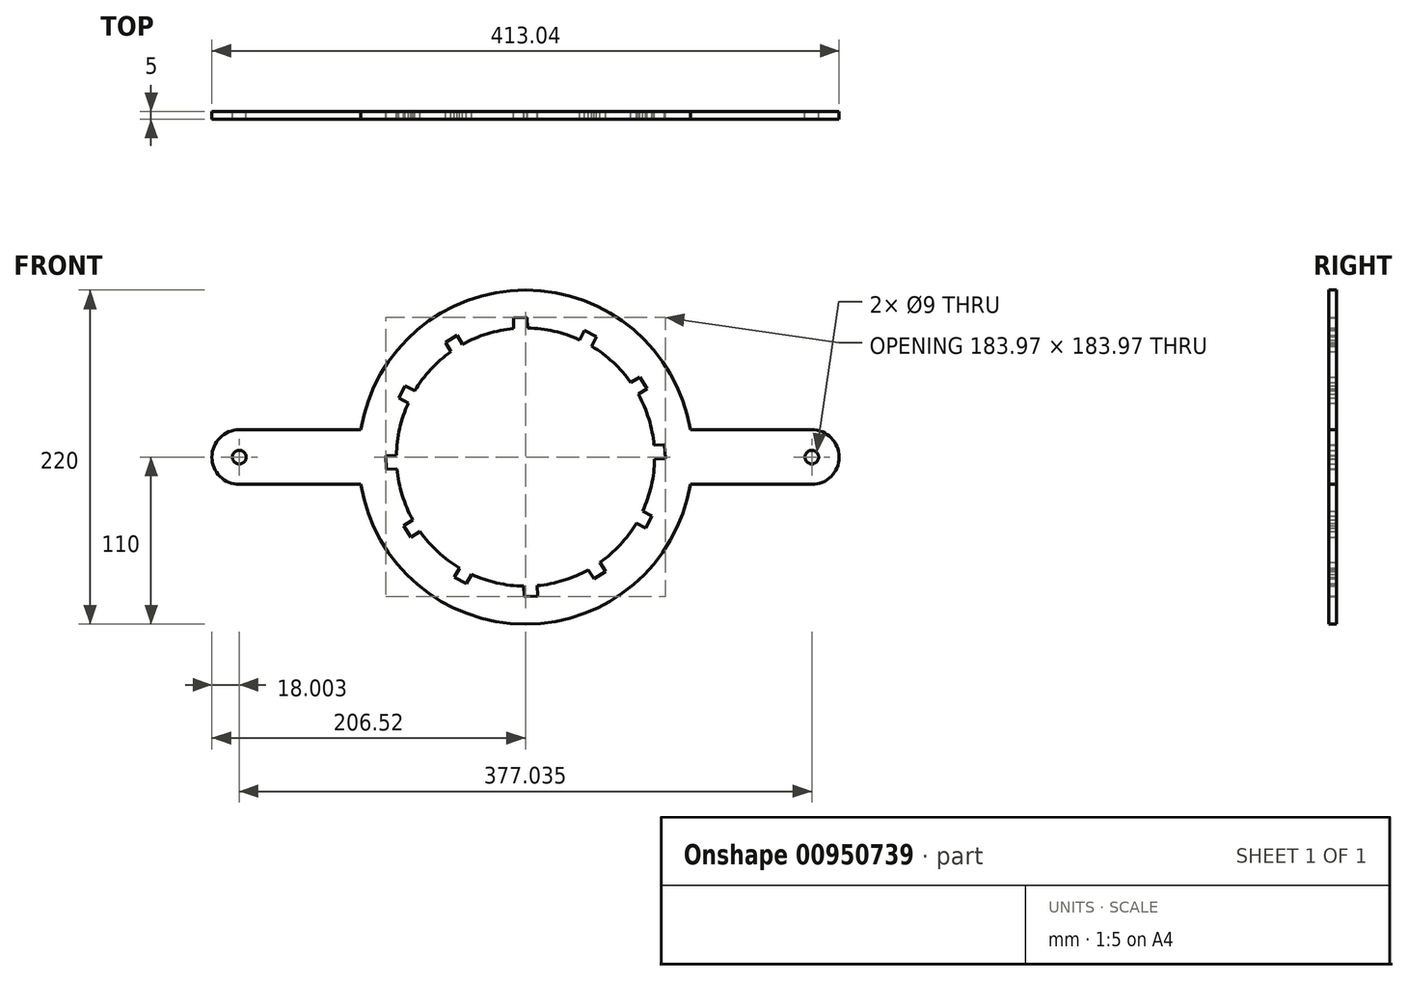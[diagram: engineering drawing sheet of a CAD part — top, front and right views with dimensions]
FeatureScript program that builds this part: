
annotation { "Feature Type Name" : "Feature", "Feature Type Description" : "" }
export const myFeature = defineFeature(function(context is Context, id is Id, definition is map)
    precondition{}
    {
        {
            var Q0;
            Q0=qCreatedBy(makeId("Front.planeOp"),FACE);
            var sketch = newSketch(context, id + "F0", { "sketchPlane" : qUnion([Q0])});
            skArc(sketch, "E0", {"start": v(-77.18, 35.61) * mm, "mid": v(-82.89, 18.84) * mm, "end": v(-85, 1.24) * mm});
            skArc(sketch, "E1", {"start": v(108.52, 18) * mm, "mid": v(0, 110) * mm, "end": v(-108.52, 18) * mm});
            skLineSegment(sketch, "E2", {"start": v(0, 235.77) * mm, "end": v(0, -237.42) * mm, "construction": true});
            skLineSegment(sketch, "E3", {"start": v(-150.79, 0) * mm, "end": v(256.18, 0) * mm, "construction": true});
            skLineSegment(sketch, "E4", {"start": v(-72.98, 43.57) * mm, "end": v(-79.17, 46.84) * mm});
            skLineSegment(sketch, "E5", {"start": v(-79.17, 46.84) * mm, "end": v(-83.37, 38.88) * mm});
            skLineSegment(sketch, "E6", {"start": v(-83.37, 38.88) * mm, "end": v(-77.18, 35.61) * mm});
            skLineSegment(sketch, "E7", {"start": v(-109.8, 57.9) * mm, "end": v(-60.63, 31.97) * mm, "construction": true});
            skLineSegment(sketch, "E8.1.0", {"start": v(-124.05, -4.76) * mm, "end": v(-68.5, -2.63) * mm, "construction": true});
            skLineSegment(sketch, "E8.1.1", {"start": v(-85, 1.24) * mm, "end": v(-91.99, 0.98) * mm});
            skLineSegment(sketch, "E8.1.2", {"start": v(-91.99, 0.98) * mm, "end": v(-91.64, -8.02) * mm});
            skLineSegment(sketch, "E8.1.3", {"start": v(-91.64, -8.02) * mm, "end": v(-84.65, -7.75) * mm});
            skLineSegment(sketch, "E8.2.0", {"start": v(-105.05, -66.15) * mm, "end": v(-58, -36.52) * mm, "construction": true});
            skLineSegment(sketch, "E8.2.1", {"start": v(-74.23, -41.42) * mm, "end": v(-80.15, -45.15) * mm});
            skLineSegment(sketch, "E8.2.2", {"start": v(-80.15, -45.15) * mm, "end": v(-75.35, -52.76) * mm});
            skLineSegment(sketch, "E8.2.3", {"start": v(-75.35, -52.76) * mm, "end": v(-69.43, -49.03) * mm});
            skLineSegment(sketch, "E8.3.0", {"start": v(-57.9, -109.8) * mm, "end": v(-31.97, -60.63) * mm, "construction": true});
            skLineSegment(sketch, "E8.3.1", {"start": v(-43.57, -72.98) * mm, "end": v(-46.84, -79.17) * mm});
            skLineSegment(sketch, "E8.3.2", {"start": v(-46.84, -79.17) * mm, "end": v(-38.88, -83.37) * mm});
            skLineSegment(sketch, "E8.3.3", {"start": v(-38.88, -83.37) * mm, "end": v(-35.61, -77.18) * mm});
            skLineSegment(sketch, "E8.4.0", {"start": v(4.76, -124.05) * mm, "end": v(2.63, -68.5) * mm, "construction": true});
            skLineSegment(sketch, "E8.4.1", {"start": v(-1.24, -85) * mm, "end": v(-0.98, -91.99) * mm});
            skLineSegment(sketch, "E8.4.2", {"start": v(-0.98, -91.99) * mm, "end": v(8.02, -91.64) * mm});
            skLineSegment(sketch, "E8.4.3", {"start": v(8.02, -91.64) * mm, "end": v(7.75, -84.65) * mm});
            skLineSegment(sketch, "E8.5.0", {"start": v(66.15, -105.05) * mm, "end": v(36.52, -58) * mm, "construction": true});
            skLineSegment(sketch, "E8.5.1", {"start": v(41.42, -74.23) * mm, "end": v(45.15, -80.15) * mm});
            skLineSegment(sketch, "E8.5.2", {"start": v(45.15, -80.15) * mm, "end": v(52.76, -75.35) * mm});
            skLineSegment(sketch, "E8.5.3", {"start": v(52.76, -75.35) * mm, "end": v(49.03, -69.43) * mm});
            skLineSegment(sketch, "E8.6.0", {"start": v(109.8, -57.9) * mm, "end": v(60.63, -31.97) * mm, "construction": true});
            skLineSegment(sketch, "E8.6.1", {"start": v(72.98, -43.57) * mm, "end": v(79.17, -46.84) * mm});
            skLineSegment(sketch, "E8.6.2", {"start": v(79.17, -46.84) * mm, "end": v(83.37, -38.88) * mm});
            skLineSegment(sketch, "E8.6.3", {"start": v(83.37, -38.88) * mm, "end": v(77.18, -35.61) * mm});
            skLineSegment(sketch, "E8.7.0", {"start": v(124.05, 4.76) * mm, "end": v(68.5, 2.63) * mm, "construction": true});
            skLineSegment(sketch, "E8.7.1", {"start": v(85, -1.24) * mm, "end": v(91.99, -0.98) * mm});
            skLineSegment(sketch, "E8.7.2", {"start": v(91.99, -0.98) * mm, "end": v(91.64, 8.02) * mm});
            skLineSegment(sketch, "E8.7.3", {"start": v(91.64, 8.02) * mm, "end": v(84.65, 7.75) * mm});
            skLineSegment(sketch, "E8.8.0", {"start": v(105.05, 66.15) * mm, "end": v(58, 36.52) * mm, "construction": true});
            skLineSegment(sketch, "E8.8.1", {"start": v(74.23, 41.42) * mm, "end": v(80.15, 45.15) * mm});
            skLineSegment(sketch, "E8.8.2", {"start": v(80.15, 45.15) * mm, "end": v(75.35, 52.76) * mm});
            skLineSegment(sketch, "E8.8.3", {"start": v(75.35, 52.76) * mm, "end": v(69.43, 49.03) * mm});
            skLineSegment(sketch, "E8.9.0", {"start": v(57.9, 109.8) * mm, "end": v(31.97, 60.63) * mm, "construction": true});
            skLineSegment(sketch, "E8.9.1", {"start": v(43.57, 72.98) * mm, "end": v(46.84, 79.17) * mm});
            skLineSegment(sketch, "E8.9.2", {"start": v(46.84, 79.17) * mm, "end": v(38.88, 83.37) * mm});
            skLineSegment(sketch, "E8.9.3", {"start": v(38.88, 83.37) * mm, "end": v(35.61, 77.18) * mm});
            skLineSegment(sketch, "E8.10.0", {"start": v(-4.76, 124.05) * mm, "end": v(-2.63, 68.5) * mm, "construction": true});
            skLineSegment(sketch, "E8.10.1", {"start": v(1.24, 85) * mm, "end": v(0.98, 91.99) * mm});
            skLineSegment(sketch, "E8.10.2", {"start": v(0.98, 91.99) * mm, "end": v(-8.02, 91.64) * mm});
            skLineSegment(sketch, "E8.10.3", {"start": v(-8.02, 91.64) * mm, "end": v(-7.75, 84.65) * mm});
            skLineSegment(sketch, "E8.11.0", {"start": v(-66.15, 105.05) * mm, "end": v(-36.52, 58) * mm, "construction": true});
            skLineSegment(sketch, "E8.11.1", {"start": v(-41.42, 74.23) * mm, "end": v(-45.15, 80.15) * mm});
            skLineSegment(sketch, "E8.11.2", {"start": v(-45.15, 80.15) * mm, "end": v(-52.76, 75.35) * mm});
            skLineSegment(sketch, "E8.11.3", {"start": v(-52.76, 75.35) * mm, "end": v(-49.03, 69.43) * mm});
            skArc(sketch, "E9.trimOffspring", {"start": v(-84.65, -7.75) * mm, "mid": v(-81.2, -25.13) * mm, "end": v(-74.23, -41.42) * mm});
            skArc(sketch, "E10.trimOffspring", {"start": v(-69.43, -49.03) * mm, "mid": v(-57.76, -62.36) * mm, "end": v(-43.57, -72.98) * mm});
            skArc(sketch, "E11.trimOffspring", {"start": v(-35.61, -77.18) * mm, "mid": v(-18.84, -82.89) * mm, "end": v(-1.24, -85) * mm});
            skArc(sketch, "E12.trimOffspring", {"start": v(7.75, -84.65) * mm, "mid": v(25.13, -81.2) * mm, "end": v(41.42, -74.23) * mm});
            skArc(sketch, "E13.trimOffspring", {"start": v(49.03, -69.43) * mm, "mid": v(62.36, -57.76) * mm, "end": v(72.98, -43.57) * mm});
            skArc(sketch, "E14.trimOffspring", {"start": v(77.18, -35.61) * mm, "mid": v(82.89, -18.84) * mm, "end": v(85, -1.24) * mm});
            skArc(sketch, "E15.trimOffspring", {"start": v(84.65, 7.75) * mm, "mid": v(81.2, 25.13) * mm, "end": v(74.23, 41.42) * mm});
            skArc(sketch, "E16.trimOffspring", {"start": v(69.43, 49.03) * mm, "mid": v(57.76, 62.36) * mm, "end": v(43.57, 72.98) * mm});
            skArc(sketch, "E17.trimOffspring", {"start": v(35.61, 77.18) * mm, "mid": v(18.84, 82.89) * mm, "end": v(1.24, 85) * mm});
            skArc(sketch, "E18.trimOffspring", {"start": v(-7.75, 84.65) * mm, "mid": v(-25.13, 81.2) * mm, "end": v(-41.42, 74.23) * mm});
            skArc(sketch, "E19.trimOffspring", {"start": v(-49.03, 69.43) * mm, "mid": v(-62.36, 57.76) * mm, "end": v(-72.98, 43.57) * mm});
            skLineSegment(sketch, "E20", {"start": v(108.52, 18) * mm, "end": v(188.52, 18) * mm});
            skLineSegment(sketch, "E21", {"start": v(188.52, -18) * mm, "end": v(108.52, -18) * mm});
            skArc(sketch, "E22", {"start": v(188.52, -18) * mm, "mid": v(206.52, 0) * mm, "end": v(188.52, 18) * mm});
            skCircle(sketch, "E23", {"center": v(188.52, 0) * mm, "radius": 4.5 * mm});
            skLineSegment(sketch, "E24.MirrorCS", {"start": v(-108.52, 18) * mm, "end": v(-188.52, 18) * mm});
            skArc(sketch, "E25.MirrorCS", {"start": v(-188.52, -18) * mm, "mid": v(-206.52, 0) * mm, "end": v(-188.52, 18) * mm});
            skLineSegment(sketch, "E26.MirrorCS", {"start": v(-188.52, -18) * mm, "end": v(-108.52, -18) * mm});
            skCircle(sketch, "E27.MirrorC", {"center": v(-188.52, 0) * mm, "radius": 4.5 * mm});
            skArc(sketch, "E28.trimOffspring", {"start": v(-108.52, -18) * mm, "mid": v(0, -110) * mm, "end": v(108.52, -18) * mm});
            skSolve(sketch);
        }
        {
            var Q0;
            Q0=makeQuery(id+"F0.imprint","IMPRINT",FACE,{"disambiguationData":[TD([[makeQuery(id+"F0.imprint","IMPRINT",EDGE,{"derivedFrom":sQuery(id+"F0.wireOp",EDGE,"E0")}),-1.0]])]});
            extrude(context, id + "F1", {"entities" : qUnion([Q0]), "depth" : 5 * mm, "offsetDistance" : 25 * mm});
        }
    });
